FCSTD DOCUMENT  (FreeCAD 0.21R33771 (Git))
Label: evalboard
License: All rights reserved
LicenseURL: https://en.wikipedia.org/wiki/All_rights_reserved
objects: Sketcher::SketchObject×1, PartDesign::Body×1
note: 2 computed .brp shape members not serialized (recipe doc carries the construction recipe); baked Part::Feature solids carry a one-line shape summary decoded from their .brp

FEATURE [Sketcher::SketchObject] Sketch001
  FullyConstrained = false
  MapMode = 5
  Support = -> [XY_Plane]
  sketch-geometry (14):
    g0: LineSegment StartX=-31.1819 StartY=127.817 StartZ=0 EndX=186.75 EndY=127.817 EndZ=0
    g1: LineSegment StartX=186.75 StartY=127.817 StartZ=0 EndX=186.75 EndY=-65.223 EndZ=0
    g2: LineSegment StartX=186.75 StartY=-65.223 StartZ=0 EndX=-31.1819 EndY=-65.223 EndZ=0
    g3: LineSegment StartX=-31.1819 StartY=-65.223 StartZ=0 EndX=-31.1819 EndY=-3.75505 EndZ=0
    g4: LineSegment StartX=-49.9779 StartY=66.603 StartZ=0 EndX=-31.1819 EndY=66.603 EndZ=0
    g5: LineSegment StartX=-31.1819 StartY=-3.75505 StartZ=0 EndX=-49.9779 EndY=-3.75505 EndZ=0
    g6: LineSegment StartX=-49.9779 StartY=-3.75505 StartZ=0 EndX=-49.9779 EndY=66.603 EndZ=0
    g7: LineSegment StartX=-31.1819 StartY=66.603 StartZ=0 EndX=-31.1819 EndY=127.817 EndZ=0
    g8: Circle CenterX=170.208 CenterY=99.877 CenterZ=0 NormalX=0 NormalY=0 NormalZ=1 AngleXU=0 Radius=1.5
    g9: Circle CenterX=170.208 CenterY=-37.283 CenterZ=0 NormalX=0 NormalY=0 NormalZ=1 AngleXU=0 Radius=1.5
    g10: GeomPoint X=186.75 Y=31.297 Z=0
    g11: Circle CenterX=63.5284 CenterY=112.577 CenterZ=0 NormalX=0 NormalY=0 NormalZ=1 AngleXU=0 Radius=1.5
    g12: Circle CenterX=63.5284 CenterY=-49.983 CenterZ=0 NormalX=0 NormalY=0 NormalZ=1 AngleXU=0 Radius=1.5
    g13: GeomPoint X=101.628 Y=31.297 Z=0
  constraints (38):
    c: Coincident(g0,g1)
    c: Coincident(g1,g2)
    c: Coincident(g2,g3)
    c: Coincident(g7,g0)
    c: Horizontal(g0)
    c: Horizontal(g2)
    c: Vertical(g1)
    c: Vertical(g3)
    c: Coincident(g5,g6)
    c: Coincident(g6,g4)
    c: Horizontal(g4)
    c: Horizontal(g5)
    c: Vertical(g6)
    c: DistanceY(g1,g1) = 193.04
    c: DistanceX(g0,g0) = 217.932
    c: Coincident(g5,g3)
    c: Coincident(g4,g7)
    c: DistanceY(g3,g3) = 61.468
    c: Parallel(g7,g1)
    c: DistanceX(g4,g4) = 18.796
    c: Equal(g2,g0)
    c: Diameter(g8) = 3
    c: Diameter(g9) = 3
    c: DistanceY(g9,g8) = 137.16
    c: DistanceY(g6,g6) = 70.358
    c: PointOnObject(g10,g1)
    c: Distance(g0,g10) = 96.52
    c: DistanceY(g10,g8) = 68.58
    c: Vertical(g8,g9)
    c: Diameter(g11) = 3
    c: DistanceY(g10,g11) = 81.28
    c: Diameter(g12) = 3
    c: Vertical(g11,g12)
    c: DistanceY(g12,g10) = 81.28
    c: DistanceX(g11,g8) = 106.68
    c: DistanceY(g13,g0) = 96.52
    c: DistanceX(g4,g13) = 151.606
    c: DistanceX(g13,g9) = 68.58
FEATURE [PartDesign::Body] Body
  Group = -> [Sketch001]
  Origin = -> Origin
